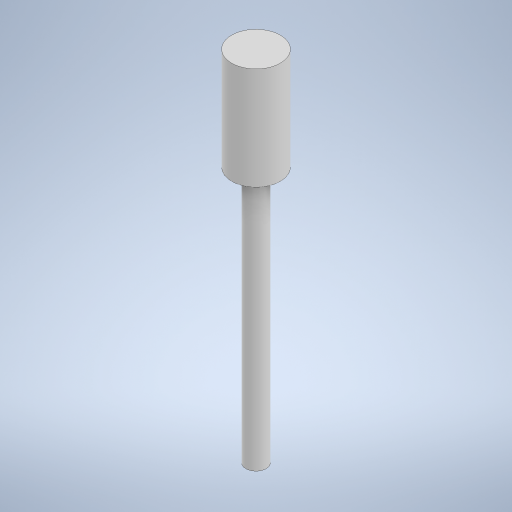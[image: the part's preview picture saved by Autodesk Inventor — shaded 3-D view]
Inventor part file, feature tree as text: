
AUTODESK INVENTOR PART (.ipt)
format: ipt  version: 2024.2 (Build 282272000, 272)  size: 236,544 bytes
history: native  units: mm
features: extrude x2, sketch x2, other x1
ambient origin geometry x8: Origin, YZ Plane, XZ Plane, XY Plane, X Axis, Y Axis, Z Axis, Center Point
bodies: Body1 (feature_tree)
feature tree (5):
  other  "ソリッド1"
  extrude  "押し出し1"  Depth=9.5mm
  extrude  "押し出し2"  Depth=20.0mm TaperAngle=0.0deg
  sketch  "スケッチ1"
  sketch  "スケッチ2"
